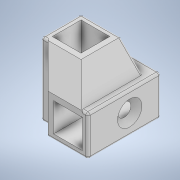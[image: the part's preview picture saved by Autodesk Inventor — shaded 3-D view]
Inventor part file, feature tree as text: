
AUTODESK INVENTOR PART (.ipt)
format: ipt  version: 2022 (Build 260153000, 153)  size: 195,584 bytes
history: native  units: in
note: dims shown in document units (in); Inventor stores cm internally (conversion verified against a paired STEP export)
features: extrude x5, sketch x5, chamfer x4, fillet x1
ambient origin geometry x8: Origin, YZ Plane, XZ Plane, XY Plane, X Axis, Y Axis, Z Axis, Center Point
bodies: Solid1 (feature_tree)
feature tree (15):
  extrude  "Extrusion1"  Depth=1.4173in
  extrude  "Extrusion2"  Depth=2.5906in
  extrude  "Extrusion3"  Depth=1.0236in TaperAngle=0.0deg
  extrude  "Extrusion4"  Depth=1.0236in
  chamfer  "Chamfer1"  Distance=2.3937in
  chamfer  "Chamfer2"  Distance=1.0236in
  extrude  "Extrusion5"  Depth=2.3937in TaperAngle=0.0deg
  chamfer  "Chamfer3"  Distance=0.7795in Angle=45.0deg
  chamfer  "Chamfer4"  Distance=0.7795in Angle=45.0deg
  fillet  "Fillet1"  Radius=0.4724in
  sketch  "Sketch1"  dims[d0=1.4173in d1=1.4173in]
  sketch  "Sketch2"  dims[d2=2.5906in d3=0.0in d4=2.5906in]
  sketch  "Sketch3"  dims[d5=1.4173in d6=1.0236in d7=0.3937in d8=0.0in d9=0.0in]
  sketch  "Sketch4"  dims[d10=1.0236in d11=1.0236in d12=2.3937in d13=0.0in]
  sketch  "Sketch5"  dims[d14=1.0236in d15=1.0236in d16=2.3937in d17=0.0in d18=0.7795in d19=0.0787in d20=45.0deg d21=0.7795in d22=0.0787in d23=45.0deg d24=0.4724in d25=2.7559in d26=0.0in d27=0.1969in d28=0.0787in d29=45.0deg d30=0.1969in d31=0.0787in d32=45.0deg d33=0.0787in]
